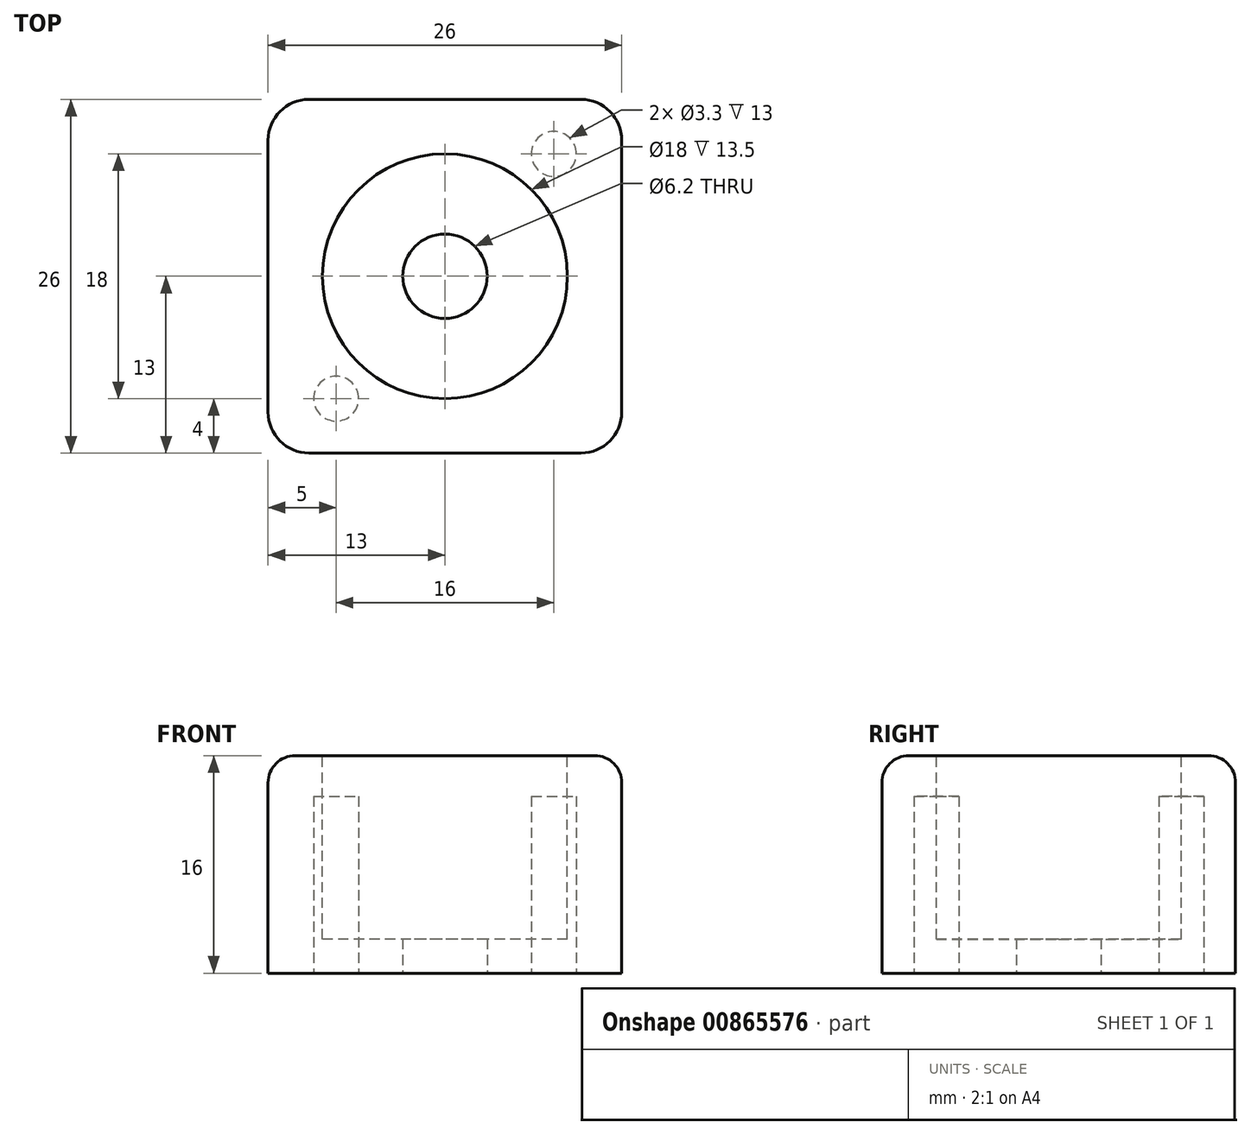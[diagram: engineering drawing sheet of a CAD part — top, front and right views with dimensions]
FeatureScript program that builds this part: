
annotation { "Feature Type Name" : "Feature", "Feature Type Description" : "" }
export const myFeature = defineFeature(function(context is Context, id is Id, definition is map)
    precondition{}
    {
        {
            var Q0;
            Q0=qCreatedBy(makeId("Top.planeOp"),FACE);
            var sketch = newSketch(context, id + "F0", { "sketchPlane" : qUnion([Q0])});
            skLineSegment(sketch, "E0.bottom", {"start": v(-13, 13) * mm, "end": v(13, 13) * mm});
            skLineSegment(sketch, "E0.top", {"start": v(-13, -13) * mm, "end": v(13, -13) * mm});
            skLineSegment(sketch, "E0.left", {"start": v(-13, 13) * mm, "end": v(-13, -13) * mm});
            skLineSegment(sketch, "E0.right", {"start": v(13, 13) * mm, "end": v(13, -13) * mm});
            skPoint(sketch, "E0.middle", {"position": v(0, 0) * mm});
            skSolve(sketch);
        }
        {
            var Q0;
            Q0=makeQuery(id+"F0.imprint","IMPRINT",FACE,{"disambiguationData":[TD([[makeQuery(id+"F0.imprint","IMPRINT",EDGE,{"derivedFrom":sQuery(id+"F0.wireOp",EDGE,"E0.bottom")}),-1.0]])]});
            extrude(context, id + "F1", {"entities" : qUnion([Q0]), "depth" : 16 * mm, "offsetDistance" : 25 * mm});
        }
        {
            var Q0;
            Q0=makeQuery(id+"F1.opExtrude","CAP_FACE",FACE,{"disambiguationData":[OSD([sQuery(id+"F0.wireOp",EDGE,"E0.bottom"),sQuery(id+"F0.wireOp",EDGE,"E0.top"),sQuery(id+"F0.wireOp",EDGE,"E0.left"),sQuery(id+"F0.wireOp",EDGE,"E0.right")])],"isStart":false});
            var sketch = newSketch(context, id + "F2", { "sketchPlane" : qUnion([Q0])});
            skCircle(sketch, "E1", {"center": v(0, 0) * mm, "radius": 9 * mm});
            skSolve(sketch);
        }
        {
            var Q0;
            Q0=makeQuery(id+"F2.imprint","IMPRINT",FACE,{"disambiguationData":[TD([[makeQuery(id+"F2.imprint","IMPRINT",EDGE,{"derivedFrom":sQuery(id+"F2.wireOp",EDGE,"E1")}),1.0]])]});
            extrude(context, id + "F3", {"entities" : qUnion([Q0]), "operationType" : NewBodyOperationType.REMOVE, "oppositeDirection" : true, "depth" : 13.5 * mm, "offsetDistance" : 25 * mm});
        }
        {
            var Q0;
            Q0=makeQuery(id+"F1.opExtrude","CAP_FACE",FACE,{"disambiguationData":[OSD([sQuery(id+"F0.wireOp",EDGE,"E0.bottom"),sQuery(id+"F0.wireOp",EDGE,"E0.top"),sQuery(id+"F0.wireOp",EDGE,"E0.left"),sQuery(id+"F0.wireOp",EDGE,"E0.right")])],"isStart":true});
            var sketch = newSketch(context, id + "F4", { "sketchPlane" : qUnion([Q0])});
            skCircle(sketch, "E2", {"center": v(0, 0) * mm, "radius": 3.1 * mm});
            skCircle(sketch, "E3", {"center": v(8, -9) * mm, "radius": 1.65 * mm});
            skCircle(sketch, "E4", {"center": v(-8, 9) * mm, "radius": 1.65 * mm});
            skSolve(sketch);
        }
        {
            var Q0;
            Q0=makeQuery(id+"F4.imprint","IMPRINT",FACE,{"disambiguationData":[TD([[makeQuery(id+"F4.imprint","IMPRINT",EDGE,{"derivedFrom":sQuery(id+"F4.wireOp",EDGE,"E3")}),1.0]])]});
            var Q1;
            Q1=makeQuery(id+"F4.imprint","IMPRINT",FACE,{"disambiguationData":[TD([[makeQuery(id+"F4.imprint","IMPRINT",EDGE,{"derivedFrom":sQuery(id+"F4.wireOp",EDGE,"E2")}),1.0]])]});
            var Q2;
            Q2=makeQuery(id+"F4.imprint","IMPRINT",FACE,{"disambiguationData":[TD([[makeQuery(id+"F4.imprint","IMPRINT",EDGE,{"derivedFrom":sQuery(id+"F4.wireOp",EDGE,"E4")}),1.0]])]});
            extrude(context, id + "F5", {"entities" : qUnion([Q0, Q1, Q2]), "operationType" : NewBodyOperationType.REMOVE, "oppositeDirection" : true, "depth" : 13 * mm, "offsetDistance" : 25 * mm});
        }
        {
            var Q0;
            Q0=makeQuery(id+"F1.opExtrude","SWEPT_EDGE",EDGE,{"disambiguationData":[OSD([sQuery(id+"F0.wireOp",EDGE,"E0.bottom"),sQuery(id+"F0.wireOp",EDGE,"E0.left")])]});
            var Q1;
            Q1=makeQuery(id+"F1.opExtrude","SWEPT_EDGE",EDGE,{"disambiguationData":[OSD([sQuery(id+"F0.wireOp",EDGE,"E0.bottom"),sQuery(id+"F0.wireOp",EDGE,"E0.right")])]});
            var Q2;
            Q2=makeQuery(id+"F1.opExtrude","SWEPT_EDGE",EDGE,{"disambiguationData":[OSD([sQuery(id+"F0.wireOp",EDGE,"E0.top"),sQuery(id+"F0.wireOp",EDGE,"E0.left")])]});
            var Q3;
            Q3=makeQuery(id+"F1.opExtrude","SWEPT_EDGE",EDGE,{"disambiguationData":[OSD([sQuery(id+"F0.wireOp",EDGE,"E0.top"),sQuery(id+"F0.wireOp",EDGE,"E0.right")])]});
            fillet(context, id + "F6", {"entities" : qUnion([Q0, Q1, Q2, Q3]), "radius" : 3 * mm, "tangentPropagation" : true, "allowEdgeOverflow" : false});
        }
        {
            var Q0;
            {var subQ0=sQuery(id+"F0.wireOp",EDGE,"E0.left");var subQ1=sQuery(id+"F0.wireOp",EDGE,"E0.top");Q0=makeQuery(id+"F6.opFillet","BLEND_EDGE",EDGE,{"blendedFrom":[makeQuery(id+"F1.opExtrude","SWEPT_EDGE",EDGE,{"disambiguationData":[OSD([subQ1,subQ0])]}),makeQuery(id+"F1.opExtrude","CAP_FACE",FACE,{"disambiguationData":[OSD([sQuery(id+"F0.wireOp",EDGE,"E0.bottom"),subQ1,subQ0,sQuery(id+"F0.wireOp",EDGE,"E0.right")])],"isStart":false})],"blendedInto":[makeQuery(id+"F1.opExtrude","CAP_FACE",FACE,{"disambiguationData":[OSD([sQuery(id+"F0.wireOp",EDGE,"E0.bottom"),subQ1,subQ0,sQuery(id+"F0.wireOp",EDGE,"E0.right")])],"isStart":false})]});}
            var Q1;
            Q1=makeQuery(id+"F1.opExtrude","CAP_EDGE",EDGE,{"disambiguationData":[OSD([sQuery(id+"F0.wireOp",EDGE,"E0.left")])],"isStart":false});
            var Q2;
            {var subQ0=sQuery(id+"F0.wireOp",EDGE,"E0.left");var subQ1=sQuery(id+"F0.wireOp",EDGE,"E0.bottom");Q2=makeQuery(id+"F6.opFillet","BLEND_EDGE",EDGE,{"blendedFrom":[makeQuery(id+"F1.opExtrude","SWEPT_EDGE",EDGE,{"disambiguationData":[OSD([subQ1,subQ0])]}),makeQuery(id+"F1.opExtrude","CAP_FACE",FACE,{"disambiguationData":[OSD([subQ1,sQuery(id+"F0.wireOp",EDGE,"E0.top"),subQ0,sQuery(id+"F0.wireOp",EDGE,"E0.right")])],"isStart":false})],"blendedInto":[makeQuery(id+"F1.opExtrude","CAP_FACE",FACE,{"disambiguationData":[OSD([subQ1,sQuery(id+"F0.wireOp",EDGE,"E0.top"),subQ0,sQuery(id+"F0.wireOp",EDGE,"E0.right")])],"isStart":false})]});}
            var Q3;
            Q3=makeQuery(id+"F1.opExtrude","CAP_EDGE",EDGE,{"disambiguationData":[OSD([sQuery(id+"F0.wireOp",EDGE,"E0.bottom")])],"isStart":false});
            var Q4;
            {var subQ0=sQuery(id+"F0.wireOp",EDGE,"E0.right");var subQ1=sQuery(id+"F0.wireOp",EDGE,"E0.bottom");Q4=makeQuery(id+"F6.opFillet","BLEND_EDGE",EDGE,{"blendedFrom":[makeQuery(id+"F1.opExtrude","SWEPT_EDGE",EDGE,{"disambiguationData":[OSD([subQ1,subQ0])]}),makeQuery(id+"F1.opExtrude","CAP_FACE",FACE,{"disambiguationData":[OSD([subQ1,sQuery(id+"F0.wireOp",EDGE,"E0.top"),sQuery(id+"F0.wireOp",EDGE,"E0.left"),subQ0])],"isStart":false})],"blendedInto":[makeQuery(id+"F1.opExtrude","CAP_FACE",FACE,{"disambiguationData":[OSD([subQ1,sQuery(id+"F0.wireOp",EDGE,"E0.top"),sQuery(id+"F0.wireOp",EDGE,"E0.left"),subQ0])],"isStart":false})]});}
            var Q5;
            Q5=makeQuery(id+"F1.opExtrude","CAP_EDGE",EDGE,{"disambiguationData":[OSD([sQuery(id+"F0.wireOp",EDGE,"E0.right")])],"isStart":false});
            var Q6;
            {var subQ0=sQuery(id+"F0.wireOp",EDGE,"E0.right");var subQ1=sQuery(id+"F0.wireOp",EDGE,"E0.top");Q6=makeQuery(id+"F6.opFillet","BLEND_EDGE",EDGE,{"blendedFrom":[makeQuery(id+"F1.opExtrude","SWEPT_EDGE",EDGE,{"disambiguationData":[OSD([subQ1,subQ0])]}),makeQuery(id+"F1.opExtrude","CAP_FACE",FACE,{"disambiguationData":[OSD([sQuery(id+"F0.wireOp",EDGE,"E0.bottom"),subQ1,sQuery(id+"F0.wireOp",EDGE,"E0.left"),subQ0])],"isStart":false})],"blendedInto":[makeQuery(id+"F1.opExtrude","CAP_FACE",FACE,{"disambiguationData":[OSD([sQuery(id+"F0.wireOp",EDGE,"E0.bottom"),subQ1,sQuery(id+"F0.wireOp",EDGE,"E0.left"),subQ0])],"isStart":false})]});}
            var Q7;
            Q7=makeQuery(id+"F1.opExtrude","CAP_EDGE",EDGE,{"disambiguationData":[OSD([sQuery(id+"F0.wireOp",EDGE,"E0.top")])],"isStart":false});
            var Q8;
            Q8=makeQuery(id+"F3.boolean.opBoolean","COPY",EDGE,{"derivedFrom":makeQuery(id+"F3.opExtrude","CAP_EDGE",EDGE,{"disambiguationData":[OSD([sQuery(id+"F2.wireOp",EDGE,"E1")])],"isStart":true})});
            fillet(context, id + "F7", {"entities" : qUnion([Q0, Q1, Q2, Q3, Q4, Q5, Q6, Q7, Q8]), "radius" : 2 * mm, "tangentPropagation" : true, "allowEdgeOverflow" : false});
        }
    });
